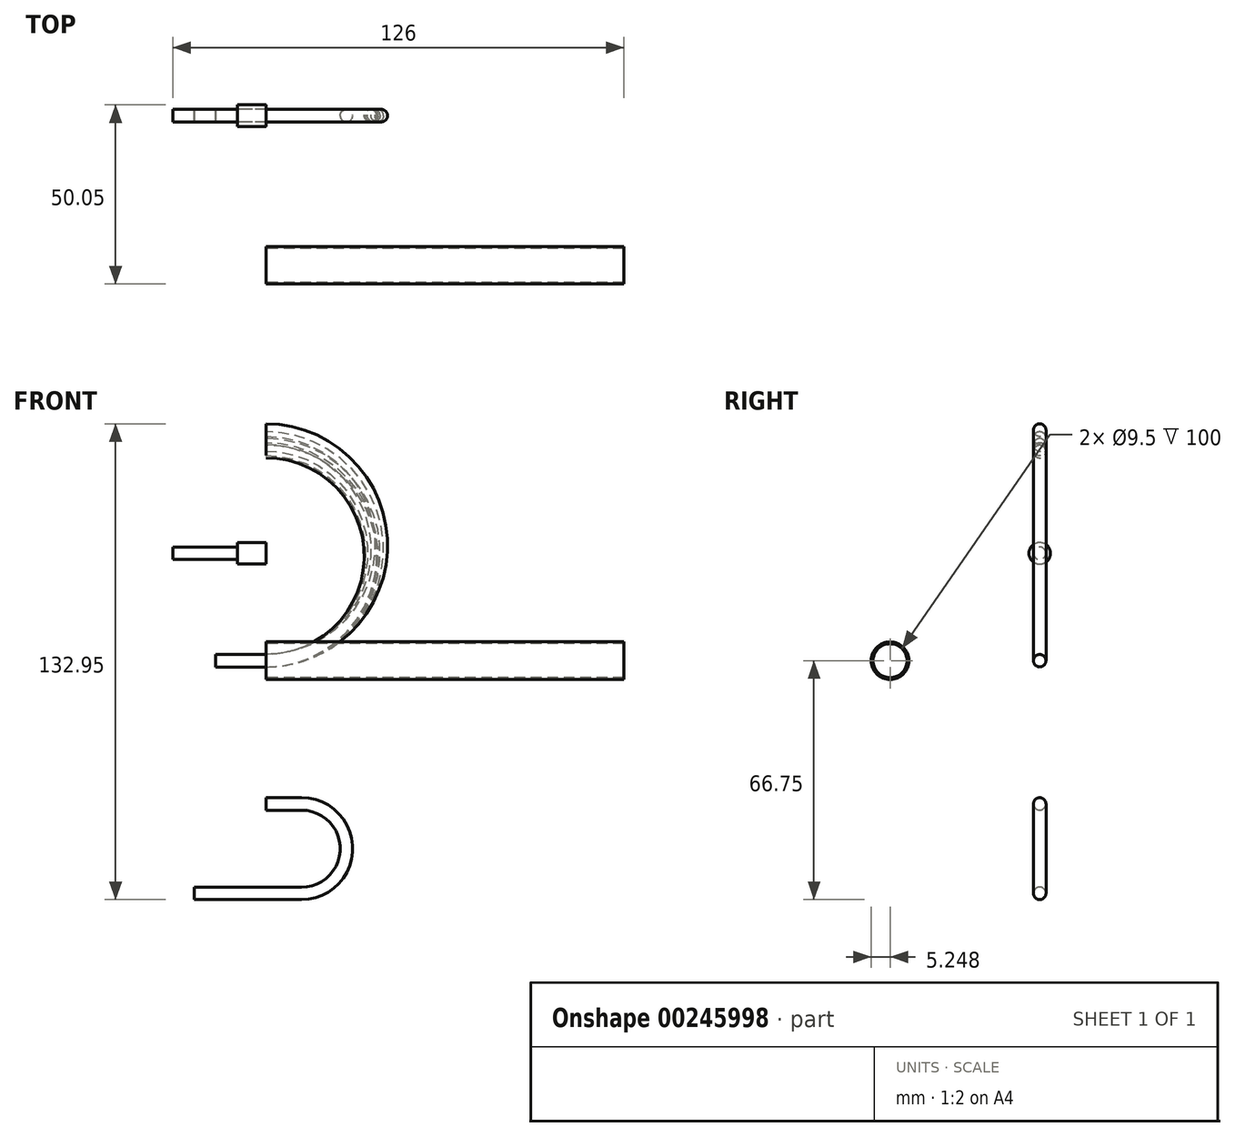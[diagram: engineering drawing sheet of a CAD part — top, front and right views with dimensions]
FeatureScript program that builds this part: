
annotation { "Feature Type Name" : "Feature", "Feature Type Description" : "" }
export const myFeature = defineFeature(function(context is Context, id is Id, definition is map)
    precondition{}
    {
        {
            var Q0;
            Q0=qCreatedBy(makeId("Front.planeOp"),FACE);
            var sketch = newSketch(context, id + "F0", { "sketchPlane" : qUnion([Q0])});
            skLineSegment(sketch, "E0", {"start": v(0, 0) * mm, "end": v(-14, 0) * mm});
            skLineSegment(sketch, "E1", {"start": v(0, 0) * mm, "end": v(0, 30) * mm, "construction": true});
            skLineSegment(sketch, "E2", {"start": v(0, 30) * mm, "end": v(-8, 30) * mm});
            skLineSegment(sketch, "E3", {"start": v(-8, 30) * mm, "end": v(-26, 30) * mm});
            skLineSegment(sketch, "E4", {"start": v(0, 0) * mm, "end": v(0, 62.2) * mm, "construction": true});
            skArc(sketch, "E5", {"start": v(0, 0) * mm, "mid": v(31.1, 31.1) * mm, "end": v(0, 62.2) * mm});
            skArc(sketch, "E6", {"start": v(0, 0) * mm, "mid": v(29.55, 29.55) * mm, "end": v(0, 59.1) * mm});
            skArc(sketch, "E7", {"start": v(0, 0) * mm, "mid": v(29.2, 29.2) * mm, "end": v(0, 58.4) * mm});
            skArc(sketch, "E8", {"start": v(0, 0) * mm, "mid": v(30.15, 30.15) * mm, "end": v(0, 60.3) * mm});
            skArc(sketch, "E9", {"start": v(0, 0) * mm, "mid": v(32.22, 32.23) * mm, "end": v(0, 64.45) * mm});
            skLineSegment(sketch, "E10", {"start": v(0, -40) * mm, "end": v(10, -40) * mm});
            skLineSegment(sketch, "E11", {"start": v(10, -40) * mm, "end": v(10, -65) * mm, "construction": true});
            skLineSegment(sketch, "E12", {"start": v(10, -65) * mm, "end": v(-20, -65) * mm});
            skArc(sketch, "E13", {"start": v(10, -65) * mm, "mid": v(22.5, -52.5) * mm, "end": v(10, -40) * mm});
            skSolve(sketch);
        }
        {
            var Q0;
            Q0=qCreatedBy(makeId("Right.planeOp"),FACE);
            var sketch = newSketch(context, id + "F1", { "sketchPlane" : qUnion([Q0])});
            skCircle(sketch, "E14", {"center": v(0, 0) * mm, "radius": 1.75 * mm});
            skCircle(sketch, "E15", {"center": v(0, 30) * mm, "radius": 1.75 * mm});
            skCircle(sketch, "E16.0", {"center": v(0, 30) * mm, "radius": 3 * mm});
            skCircle(sketch, "E17", {"center": v(-41.8, 0) * mm, "radius": 5.25 * mm});
            skCircle(sketch, "E18.0", {"center": v(-41.8, 0) * mm, "radius": 4.75 * mm});
            skCircle(sketch, "E19", {"center": v(0, -40) * mm, "radius": 1.75 * mm});
            skSolve(sketch);
        }
        {
            var Q0;
            Q0=makeQuery(id+"F1.imprint","IMPRINT",FACE,{"disambiguationData":[TD([[makeQuery(id+"F1.imprint","IMPRINT",EDGE,{"derivedFrom":sQuery(id+"F1.wireOp",EDGE,"E15")}),-1.0]])]});
            var Q1;
            Q1=sQuery(id+"F1.wireOp",EDGE,"E16.0");
            var Q2;
            Q2=sQuery(id+"F0.wireOp",EDGE,"E2");
            sweep(context, id + "F2", {"profiles" : qUnion([Q0]), "surfaceProfiles" : qUnion([Q1]), "path" : qUnion([Q2])});
        }
        {
            var Q0;
            Q0=makeQuery(id+"F1.imprint","IMPRINT",FACE,{"disambiguationData":[TD([[makeQuery(id+"F1.imprint","IMPRINT",EDGE,{"derivedFrom":sQuery(id+"F1.wireOp",EDGE,"E15")}),1.0]])]});
            var Q1;
            Q1=sQuery(id+"F0.wireOp",EDGE,"E3");
            var Q2;
            Q2=sQuery(id+"F0.wireOp",EDGE,"E2");
            sweep(context, id + "F3", {"operationType" : NewBodyOperationType.ADD, "profiles" : qUnion([Q0]), "path" : qUnion([Q1, Q2])});
        }
        {
            var Q0;
            Q0=makeQuery(id+"F1.imprint","IMPRINT",FACE,{"disambiguationData":[TD([[makeQuery(id+"F1.imprint","IMPRINT",EDGE,{"derivedFrom":sQuery(id+"F1.wireOp",EDGE,"E14")}),1.0]])]});
            var Q1;
            Q1=sQuery(id+"F0.wireOp",EDGE,"E0");
            sweep(context, id + "F4", {"profiles" : qUnion([Q0]), "path" : qUnion([Q1])});
        }
        {
            var Q0;
            Q0=makeQuery(id+"F1.imprint","IMPRINT",FACE,{"disambiguationData":[TD([[makeQuery(id+"F1.imprint","IMPRINT",EDGE,{"derivedFrom":sQuery(id+"F1.wireOp",EDGE,"E14")}),1.0]])]});
            var Q1;
            Q1=sQuery(id+"F0.wireOp",EDGE,"E5");
            sweep(context, id + "F5", {"profiles" : qUnion([Q0]), "path" : qUnion([Q1])});
        }
        {
            var Q0;
            Q0=makeQuery(id+"F1.imprint","IMPRINT",FACE,{"disambiguationData":[TD([[makeQuery(id+"F1.imprint","IMPRINT",EDGE,{"derivedFrom":sQuery(id+"F1.wireOp",EDGE,"E14")}),1.0]])]});
            var Q1;
            Q1=sQuery(id+"F1.wireOp",EDGE,"E14");
            var Q2;
            Q2=sQuery(id+"F0.wireOp",EDGE,"E6");
            sweep(context, id + "F6", {"profiles" : qUnion([Q0]), "surfaceProfiles" : qUnion([Q1]), "path" : qUnion([Q2])});
        }
        {
            var Q0;
            Q0=makeQuery(id+"F1.imprint","IMPRINT",FACE,{"disambiguationData":[TD([[makeQuery(id+"F1.imprint","IMPRINT",EDGE,{"derivedFrom":sQuery(id+"F1.wireOp",EDGE,"E14")}),1.0]])]});
            var Q1;
            Q1=sQuery(id+"F1.wireOp",EDGE,"E14");
            var Q2;
            Q2=sQuery(id+"F0.wireOp",EDGE,"E7");
            sweep(context, id + "F7", {"profiles" : qUnion([Q0]), "surfaceProfiles" : qUnion([Q1]), "path" : qUnion([Q2])});
        }
        {
            var Q0;
            Q0=makeQuery(id+"F1.imprint","IMPRINT",FACE,{"disambiguationData":[TD([[makeQuery(id+"F1.imprint","IMPRINT",EDGE,{"derivedFrom":sQuery(id+"F1.wireOp",EDGE,"E14")}),1.0]])]});
            var Q1;
            Q1=sQuery(id+"F0.wireOp",EDGE,"E8");
            sweep(context, id + "F8", {"profiles" : qUnion([Q0]), "path" : qUnion([Q1])});
        }
        {
            var Q0;
            Q0=makeQuery(id+"F1.imprint","IMPRINT",FACE,{"disambiguationData":[TD([[makeQuery(id+"F1.imprint","IMPRINT",EDGE,{"derivedFrom":sQuery(id+"F1.wireOp",EDGE,"E14")}),1.0]])]});
            var Q1;
            Q1=sQuery(id+"F0.wireOp",EDGE,"E9");
            sweep(context, id + "F9", {"profiles" : qUnion([Q0]), "path" : qUnion([Q1])});
        }
        {
            var Q0;
            Q0=makeQuery(id+"F1.imprint","IMPRINT",FACE,{"disambiguationData":[TD([[makeQuery(id+"F1.imprint","IMPRINT",EDGE,{"derivedFrom":sQuery(id+"F1.wireOp",EDGE,"E17")}),1.0]])]});
            extrude(context, id + "F10", {"entities" : qUnion([Q0]), "depth" : 100 * mm, "offsetDistance" : 25 * mm});
        }
        {
            var Q0;
            Q0=makeQuery(id+"F1.imprint","IMPRINT",FACE,{"disambiguationData":[TD([[makeQuery(id+"F1.imprint","IMPRINT",EDGE,{"derivedFrom":sQuery(id+"F1.wireOp",EDGE,"E19")}),1.0]])]});
            var Q1;
            Q1=sQuery(id+"F0.wireOp",EDGE,"E10");
            var Q2;
            Q2=sQuery(id+"F0.wireOp",EDGE,"E13");
            var Q3;
            Q3=sQuery(id+"F0.wireOp",EDGE,"E12");
            sweep(context, id + "F11", {"profiles" : qUnion([Q0]), "path" : qUnion([Q1, Q2, Q3])});
        }
        {
            var Q0;
            Q0=makeQuery(id+"F1.imprint","IMPRINT",FACE,{"disambiguationData":[TD([[makeQuery(id+"F1.imprint","IMPRINT",EDGE,{"derivedFrom":sQuery(id+"F1.wireOp",EDGE,"E19")}),1.0]])]});
            var Q1;
            Q1=sQuery(id+"F0.wireOp",EDGE,"E10");
            var Q2;
            Q2=sQuery(id+"F0.wireOp",EDGE,"E13");
            var Q3;
            Q3=sQuery(id+"F0.wireOp",EDGE,"E12");
            sweep(context, id + "F12", {"profiles" : qUnion([Q0]), "path" : qUnion([Q1, Q2, Q3])});
        }
        {
            var Q0;
            Q0=makeQuery(id+"F1.imprint","IMPRINT",FACE,{"disambiguationData":[TD([[makeQuery(id+"F1.imprint","IMPRINT",EDGE,{"derivedFrom":sQuery(id+"F1.wireOp",EDGE,"E17")}),1.0]])]});
            var Q1;
            Q1=sQuery(id+"F1.wireOp",EDGE,"E17");
            var Q2;
            Q2=sQuery(id+"F1.wireOp",EDGE,"E18.0");
            extrude(context, id + "F13", {"entities" : qUnion([Q0]), "surfaceEntities" : qUnion([Q1, Q2]), "depth" : 100 * mm, "offsetDistance" : 25 * mm});
        }
    });
